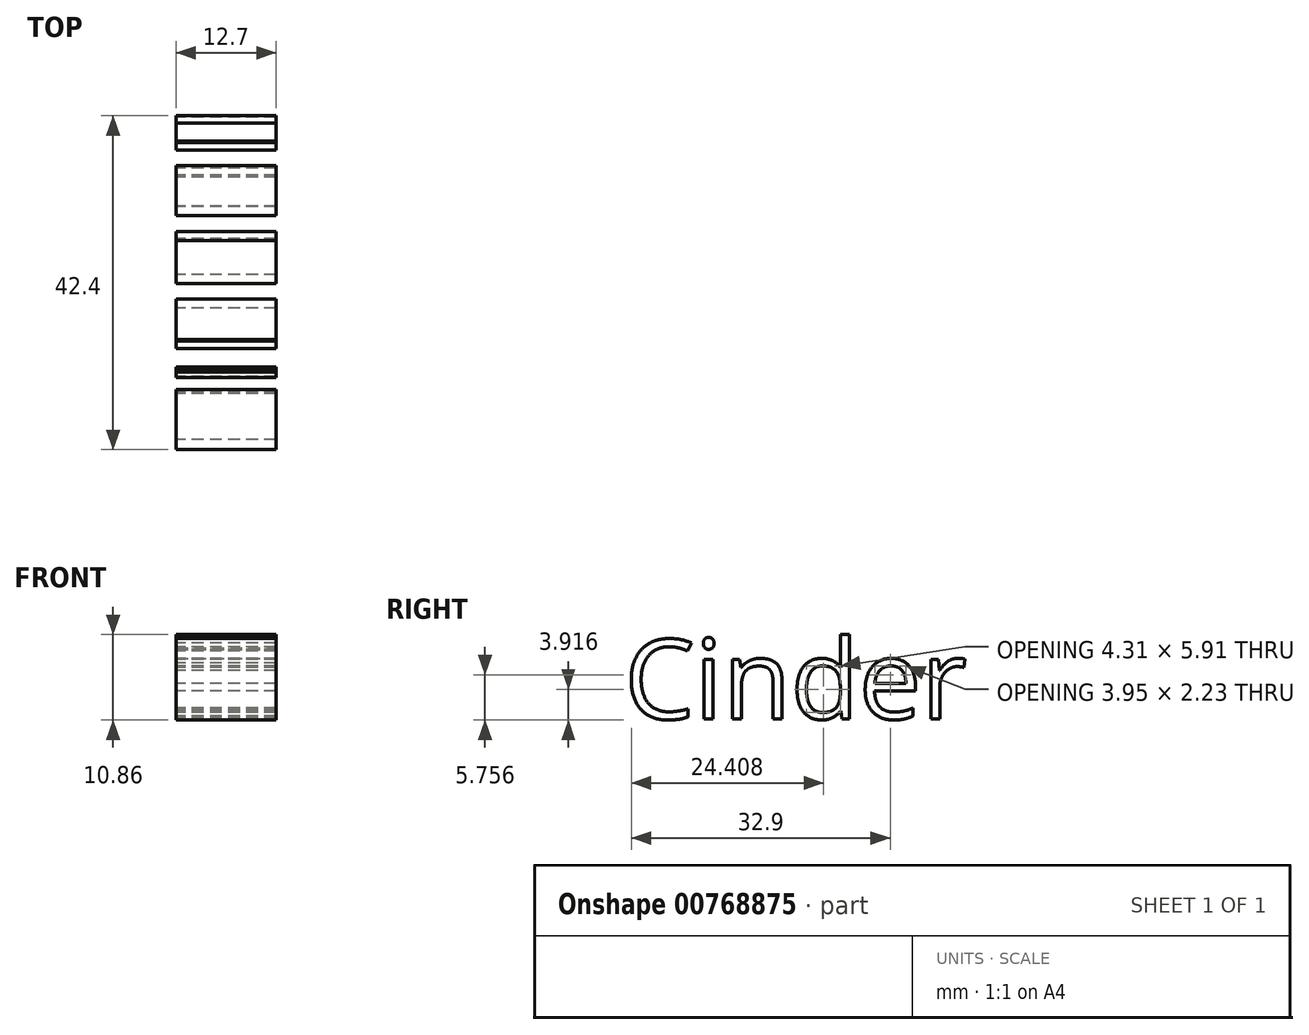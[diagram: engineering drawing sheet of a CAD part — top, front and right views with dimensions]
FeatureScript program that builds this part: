
annotation { "Feature Type Name" : "Feature", "Feature Type Description" : "" }
export const myFeature = defineFeature(function(context is Context, id is Id, definition is map)
    precondition{}
    {
        {
            var Q0;
            Q0=qCreatedBy(makeId("Right.planeOp"),FACE);
            var sketch = newSketch(context, id + "F0", { "sketchPlane" : qUnion([Q0])});
            skText(sketch, "E0", { "text": "Cinder\n", "fontName": "OpenSans-Regular.ttf"});
            const initialGuessF0  = {"E0": [-0.02776, 0.01399, 1, 0, 0.01016]};
            skSetInitialGuess(sketch, initialGuessF0);
            skSolve(sketch);
        }
        {
            var Q0;
            Q0 = qSketchRegion(id + "F0", true);
            extrude(context, id + "F1", {"entities" : qUnion([Q0]), "depth" : 12.7 * mm, "offsetDistance" : 25.4 * mm});
        }
    });
